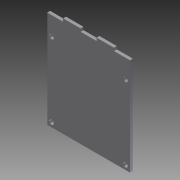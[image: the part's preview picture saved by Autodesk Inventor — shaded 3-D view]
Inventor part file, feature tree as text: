
AUTODESK INVENTOR PART (.ipt)
format: ipt  version: 2012 (Build 160160000, 160)  size: 111,104 bytes
history: native  units: mm
features: sketch x2, extrude x1, hole x1
ambient origin geometry x8: Origin, YZ Plane, XZ Plane, XY Plane, X Axis, Y Axis, Z Axis, Center Point
bodies: Solid1 (feature_tree)
feature tree (4):
  extrude  "Extrusion1"  Depth=2.0mm TaperAngle=0.0deg
  hole  "Hole1"  [1 undecoded]
  sketch  "Sketch1"  dims[d0=57.0mm d1=67.0mm d2=3.0mm d3=3.0mm d4=3.0mm d5=51.0mm d6=51.0mm d7=51.0mm d8=51.0mm d9=3.0mm d10=2.0mm d11=12.0mm d12=12.0mm d13=11.0mm d14=11.0mm d15=3.0mm d16=3.0mm d17=3.0mm d18=2.0mm d19=0.0mm]
  sketch  "Sketch2"  dims[d20=57.0mm d21=67.0mm d22=3.0mm d23=3.0mm d24=3.0mm d25=51.0mm d26=51.0mm d27=51.0mm d28=51.0mm d29=3.0mm d30=2.0mm d31=12.0mm d32=12.0mm d33=11.0mm d34=11.0mm d35=3.0mm d36=3.0mm d37=3.0mm d38=3.0mm d39=6.0mm d40=4.0mm d41=2.0mm d42=90.0deg d43=8.0mm d44=20.594885mm]
note: 1 required parameter value undecoded (feature->parameter linkage not recoverable at this tier; creation-order binding heuristic only, values carry confidence <= 0.55)
